# Revit family: BVN_BDKF-R
name_source: partatom
category: Mechanical Equipment
units: mm (PartAtom-declared; Revit-internal decimal feet)

## family parameters
Always vertical = Yes
Cut with Voids When Loaded = No
OmniClass Number = 23.75.00.00
OmniClass Title = Climate Control (HVAC)
Part Type = Breaks Into
Room Calculation Point = No
Round Connector Dimension = Use Diameter
Shared = No
Work Plane-Based = No

## types (12) — shared parameters
Corners = 20 mm  [stored 0.0656168 ft]
Description = Duct Fan
Frequency = 50 Hz
Insulation Class = F
Manufacturer = Bahçıvan Elektrik Motor San. ve Tic. Ltd. Şti.
Material = <By Category>
Model = BDKF-R
Protection Class = 55
Sac = -2 mm  [stored -0.00656168 ft]
URL = http://www.bahcivanmotor.com.tr
motor_x = 100 mm  [stored 0.328084 ft]
motor_y = 100 mm  [stored 0.328084 ft]

## per-type parameters (varying)
| type | 150 | 180 | A | Air Flow | B | C | Capacitor | Current | D | E | F | G | Power | Sound Pressure Level dB(A) | Speed ( d/d ) | Voltage | Weight |
| BDKF-R 315M | Yes | No | 350 mm  [stored 1.14829 ft] | 2000.0 m³/h | 600 mm | 760 mm | 10 | 2 A | 620 mm  [stored 2.03412 ft] | 370 mm  [stored 1.21391 ft] | 650 mm  [stored 2.13255 ft] | 400 mm  [stored 1.31234 ft] | 250 W | 53 | 1380 | 230 V | 35.00 kg |
| BDKF-R 355M | Yes | No | 350 mm  [stored 1.14829 ft] | 3000.0 m³/h | 600 mm | 760 mm | 10 | 2 A | 620 mm  [stored 2.03412 ft] | 370 mm  [stored 1.21391 ft] | 650 mm  [stored 2.13255 ft] | 400 mm  [stored 1.31234 ft] | 25 W | 58 | 1380 | 230 V | 36.00 kg |
| BDKF-R 400M | Yes | No | 400 mm  [stored 1.31234 ft] | 4100.0 m³/h | 700 mm  [stored 2.29659 ft] | 800 mm  [stored 2.62467 ft] | 15 | 3 A | 720 mm  [stored 2.3622 ft] | 420 mm  [stored 1.37795 ft] | 750 mm  [stored 2.46063 ft] | 450 mm  [stored 1.47638 ft] | 370 W | 56 | 1390 | 230 V | 49.00 kg |
| BDKF-R 450M | No | Yes | 400 mm  [stored 1.31234 ft] | 5500.0 m³/h | 700 mm  [stored 2.29659 ft] | 800 mm  [stored 2.62467 ft] | 20 | 5 A | 720 mm  [stored 2.3622 ft] | 420 mm  [stored 1.37795 ft] | 750 mm  [stored 2.46063 ft] | 450 mm  [stored 1.47638 ft] | 550 W | 58 | 1395 | 230 V | 52.00 kg |
| BDKF-R 500M | No | Yes | 500 mm  [stored 1.64042 ft] | 8100.0 m³/h | 800 mm  [stored 2.62467 ft] | 920 mm  [stored 3.01837 ft] | 35 | 8 A | 820 mm  [stored 2.69029 ft] | 520 mm  [stored 1.70604 ft] | 850 mm  [stored 2.78871 ft] | 560 mm  [stored 1.83727 ft] | 1100 W | 64 | 1410 | 230 V | 74.00 kg |
| BDKF-R 560M | No | Yes | 500 mm  [stored 1.64042 ft] | 10500.0 m³/h | 1000 mm  [stored 3.28084 ft] | 1050 mm  [stored 3.44488 ft] | 50 | 14 A | 1030 mm  [stored 3.37927 ft] | 530 mm  [stored 1.73885 ft] | 1060 mm  [stored 3.47769 ft] | 560 mm  [stored 1.83727 ft] | 2200 W | 66 | 1420 | 230 V | 91.00 kg |
| BDKF-R 315T | Yes | No | 350 mm  [stored 1.14829 ft] | 2000.0 m³/h | 600 mm | 760 mm | 0 | 1 A | 620 mm  [stored 2.03412 ft] | 370 mm  [stored 1.21391 ft] | 650 mm  [stored 2.13255 ft] | 400 mm  [stored 1.31234 ft] | 250 W | 53 | 1380 | 380 V | 35.00 kg |
| BDKF-R 355T | Yes | No | 350 mm  [stored 1.14829 ft] | 3000.0 m³/h | 600 mm | 760 mm | 0 | 1 A | 620 mm  [stored 2.03412 ft] | 370 mm  [stored 1.21391 ft] | 650 mm  [stored 2.13255 ft] | 400 mm  [stored 1.31234 ft] | 25 W | 58 | 1380 | 380 V | 36.00 kg |
| BDKF-R 400T | Yes | No | 400 mm  [stored 1.31234 ft] | 4100.0 m³/h | 700 mm  [stored 2.29659 ft] | 800 mm  [stored 2.62467 ft] | 0 | 1 A | 720 mm  [stored 2.3622 ft] | 420 mm  [stored 1.37795 ft] | 750 mm  [stored 2.46063 ft] | 450 mm  [stored 1.47638 ft] | 370 W | 56 | 1390 | 380 V | 49.00 kg |
| BDKF-R 450T | No | Yes | 400 mm  [stored 1.31234 ft] | 5500.0 m³/h | 700 mm  [stored 2.29659 ft] | 800 mm  [stored 2.62467 ft] | 0 | 2 A | 720 mm  [stored 2.3622 ft] | 420 mm  [stored 1.37795 ft] | 750 mm  [stored 2.46063 ft] | 450 mm  [stored 1.47638 ft] | 550 W | 58 | 1395 | 380 V | 52.00 kg |
| BDKF-R 500T | No | Yes | 500 mm  [stored 1.64042 ft] | 8100.0 m³/h | 800 mm  [stored 2.62467 ft] | 920 mm  [stored 3.01837 ft] | 0 | 3 A | 820 mm  [stored 2.69029 ft] | 520 mm  [stored 1.70604 ft] | 850 mm  [stored 2.78871 ft] | 560 mm  [stored 1.83727 ft] | 1100 W | 64 | 1410 | 380 V | 74.00 kg |
| BDKF-R 560T | No | Yes | 500 mm  [stored 1.64042 ft] | 10500.0 m³/h | 1000 mm  [stored 3.28084 ft] | 1050 mm  [stored 3.44488 ft] | 50 | 5 A | 1030 mm  [stored 3.37927 ft] | 530 mm  [stored 1.73885 ft] | 1060 mm  [stored 3.47769 ft] | 560 mm  [stored 1.83727 ft] | 2200 W | 66 | 1420 | 380 V | 91.00 kg |

note: [stored X ft] marks values corroborated as IEEE doubles in the binary element streams (Revit-internal decimal feet)

## geometry (parser evidence)
native form markers: Sweep x2
no freeform markers — native parametric forms only
